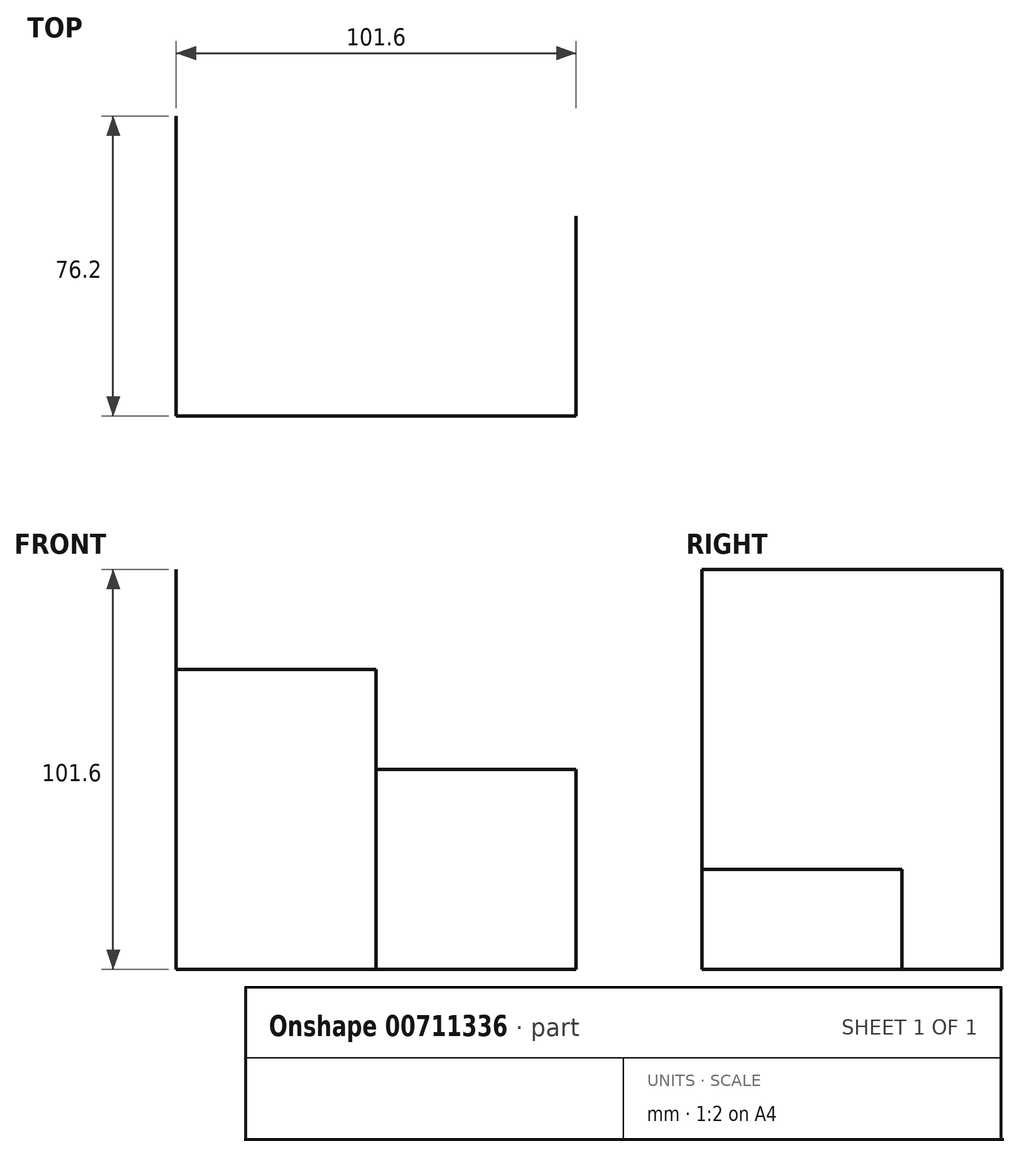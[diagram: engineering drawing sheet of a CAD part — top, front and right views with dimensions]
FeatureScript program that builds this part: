
annotation { "Feature Type Name" : "Feature", "Feature Type Description" : "" }
export const myFeature = defineFeature(function(context is Context, id is Id, definition is map)
    precondition{}
    {
        {
            var Q0;
            Q0=qCreatedBy(makeId("Top.planeOp"),FACE);
            var sketch = newSketch(context, id + "F0", { "sketchPlane" : qUnion([Q0])});
            skPoint(sketch, "E0", {"position": v(56.85, 0) * mm});
            skPoint(sketch, "E1", {"position": v(56.85, -50.8) * mm});
            skLineSegment(sketch, "E2", {"start": v(56.85, 0) * mm, "end": v(56.85, -50.8) * mm});
            skLineSegment(sketch, "E3", {"start": v(56.85, -50.8) * mm, "end": v(6.05, -50.8) * mm});
            skLineSegment(sketch, "E4", {"start": v(-44.75, -50.8) * mm, "end": v(-44.75, -50.8) * mm});
            skLineSegment(sketch, "E5", {"start": v(56.85, -50.8) * mm, "end": v(56.85, -50.8) * mm});
            skPoint(sketch, "E6", {"position": v(6.05, -50.8) * mm});
            skPoint(sketch, "E7", {"position": v(-44.75, -50.8) * mm});
            skLineSegment(sketch, "E8", {"start": v(-44.75, -50.8) * mm, "end": v(-44.75, 25.4) * mm});
            skLineSegment(sketch, "E9", {"start": v(6.05, -50.8) * mm, "end": v(-44.75, -50.8) * mm});
            skSolve(sketch);
        }
        {
            var Q0;
            Q0=sQuery(id+"F0.wireOp",EDGE,"E8");
            extrude(context, id + "F1", {"bodyType" : ToolBodyType.SURFACE, "surfaceEntities" : qUnion([Q0]), "depth" : 101.6 * mm, "offsetDistance" : 25.4 * mm});
        }
        {
            var Q0;
            Q0=sQuery(id+"F0.wireOp",EDGE,"E9");
            extrude(context, id + "F2", {"bodyType" : ToolBodyType.SURFACE, "surfaceEntities" : qUnion([Q0]), "depth" : 76.2 * mm, "offsetDistance" : 25.4 * mm});
        }
        {
            var Q0;
            Q0=sQuery(id+"F0.wireOp",EDGE,"E3");
            extrude(context, id + "F3", {"bodyType" : ToolBodyType.SURFACE, "surfaceEntities" : qUnion([Q0]), "depth" : 50.8 * mm, "offsetDistance" : 25.4 * mm});
        }
        {
            var Q0;
            Q0=sQuery(id+"F0.wireOp",EDGE,"E2");
            extrude(context, id + "F4", {"bodyType" : ToolBodyType.SURFACE, "surfaceEntities" : qUnion([Q0]), "depth" : 25.4 * mm, "offsetDistance" : 25.4 * mm});
        }
    });
